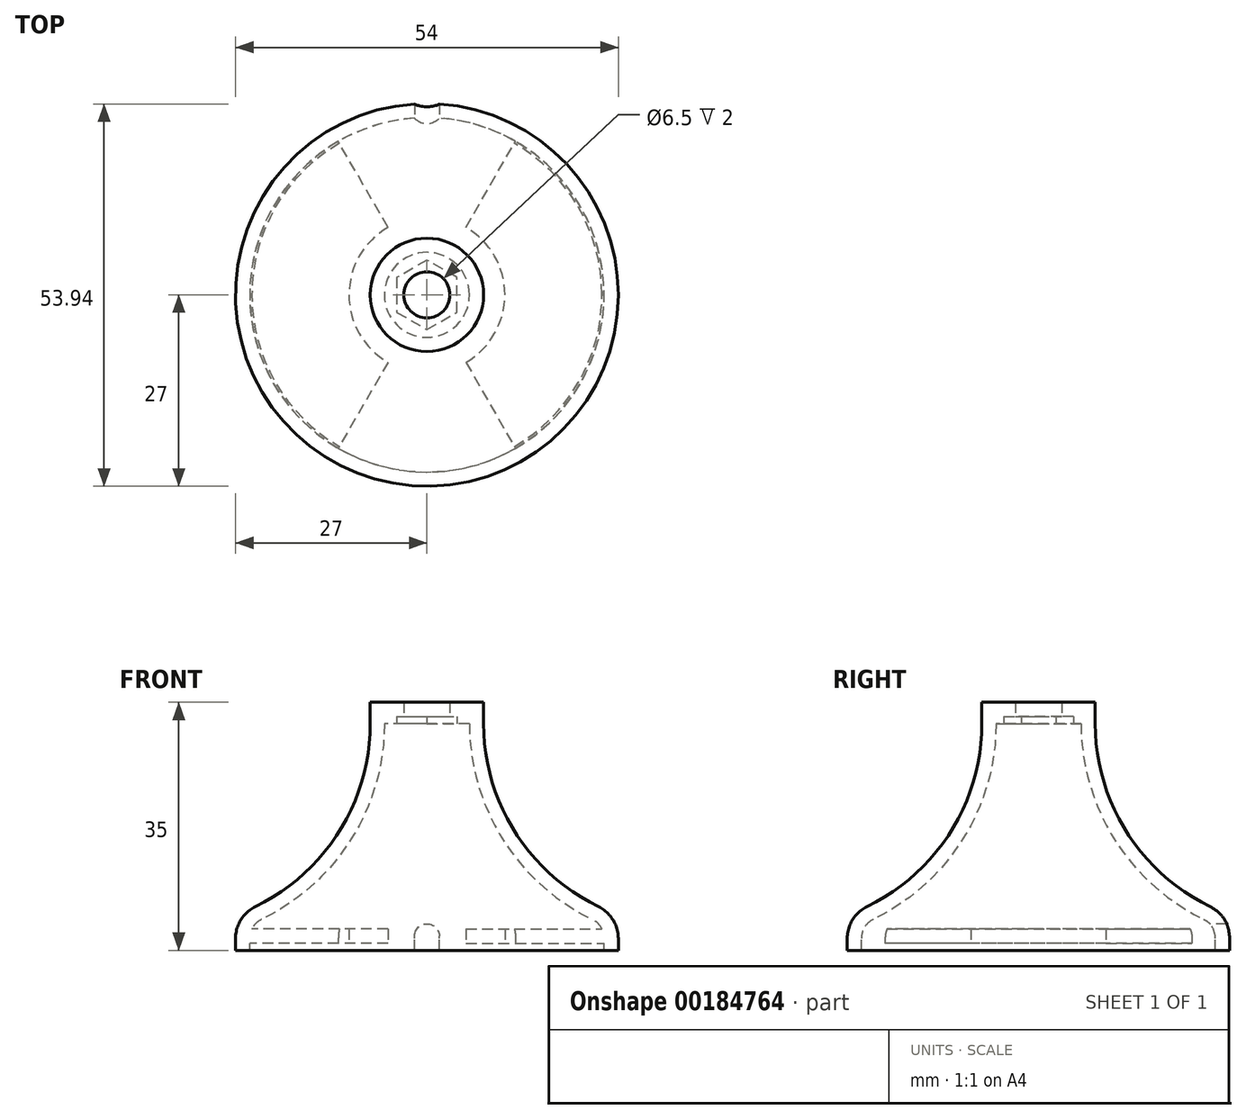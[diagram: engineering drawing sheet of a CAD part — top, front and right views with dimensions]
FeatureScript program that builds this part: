
annotation { "Feature Type Name" : "Feature", "Feature Type Description" : "" }
export const myFeature = defineFeature(function(context is Context, id is Id, definition is map)
    precondition{}
    {
        {
            var Q0;
            Q0=qCreatedBy(makeId("Front.planeOp"),FACE);
            var sketch = newSketch(context, id + "F0", { "sketchPlane" : qUnion([Q0])});
            skLineSegment(sketch, "E0", {"start": v(0, 35) * mm, "end": v(-8, 35) * mm});
            skLineSegment(sketch, "E1", {"start": v(-8, 35) * mm, "end": v(-8, 32) * mm});
            skLineSegment(sketch, "E2", {"start": v(0, 0) * mm, "end": v(-27, 0) * mm, "construction": true});
            skLineSegment(sketch, "E3", {"start": v(-27, 0) * mm, "end": v(-27, 1.68) * mm});
            skLineSegment(sketch, "E4", {"start": v(0, 35) * mm, "end": v(0, 0) * mm, "construction": true});
            skArc(sketch, "E5", {"start": v(-24.18, 6.18) * mm, "mid": v(-12.38, 16.77) * mm, "end": v(-8, 32) * mm});
            skPoint(sketch, "E6.visualSharp", {"position": v(-27, 5) * mm});
            skArc(sketch, "E6.filletArc", {"start": v(-24.18, 6.18) * mm, "mid": v(-26.24, 4.34) * mm, "end": v(-27, 1.68) * mm});
            skLineSegment(sketch, "E7", {"start": v(0, 35) * mm, "end": v(0, 32) * mm});
            skLineSegment(sketch, "E8.0", {"start": v(-25, 0) * mm, "end": v(-25, 1.68) * mm});
            skArc(sketch, "E8.1", {"start": v(-23.3, 4.38) * mm, "mid": v(-10.68, 15.7) * mm, "end": v(-6, 32) * mm});
            skLineSegment(sketch, "E8.2", {"start": v(0, 33) * mm, "end": v(-6.02, 33) * mm, "construction": true});
            skLineSegment(sketch, "E9", {"start": v(-27, 0) * mm, "end": v(-25, 0) * mm});
            skPoint(sketch, "E10.visualSharp", {"position": v(-25, 3.63) * mm});
            skArc(sketch, "E10.filletArc", {"start": v(-23.3, 4.38) * mm, "mid": v(-24.54, 3.28) * mm, "end": v(-25, 1.68) * mm});
            skLineSegment(sketch, "E11", {"start": v(0, 32) * mm, "end": v(-6, 32) * mm});
            skSolve(sketch);
        }
        {
            var Q0;
            Q0 = qSketchRegion(id + "F0", true);
            var Q1;
            Q1=sQuery(id+"F0.wireOp",EDGE,"E4");
            revolve(context, id + "F1", {"entities" : qUnion([Q0]), "axis" : qUnion([Q1]), "revolveType" : RevolveType.FULL});
        }
        {
            var Q0;
            Q0=makeQuery(id+"F1.opRevolve","SWEPT_FACE",FACE,{"disambiguationData":[OSD([sQuery(id+"F0.wireOp",EDGE,"E11")])]});
            var sketch = newSketch(context, id + "F2", { "sketchPlane" : qUnion([Q0])});
            skCircle(sketch, "E12.cCircle", {"center": v(0, 0) * mm, "radius": 4.25 * mm, "construction": true});
            skLineSegment(sketch, "E12.0", {"start": v(4.25, 2.45) * mm, "end": v(4.25, -2.45) * mm});
            skLineSegment(sketch, "E12.1", {"start": v(4.25, -2.45) * mm, "end": v(0, -4.9) * mm});
            skLineSegment(sketch, "E12.2", {"start": v(0, -4.9) * mm, "end": v(-4.25, -2.45) * mm});
            skLineSegment(sketch, "E12.3", {"start": v(-4.25, -2.45) * mm, "end": v(-4.25, 2.45) * mm});
            skLineSegment(sketch, "E12.4", {"start": v(-4.25, 2.45) * mm, "end": v(0, 4.9) * mm});
            skLineSegment(sketch, "E12.5", {"start": v(0, 4.9) * mm, "end": v(4.25, 2.45) * mm});
            skPoint(sketch, "E12.0.midPoint", {"position": v(4.25, 0) * mm});
            skSolve(sketch);
        }
        {
            var Q0;
            Q0 = qSketchRegion(id + "F2", true);
            extrude(context, id + "F3", {"entities" : qUnion([Q0]), "operationType" : NewBodyOperationType.REMOVE, "oppositeDirection" : true, "depth" : 1 * mm});
        }
        {
            var Q0;
            Q0=makeQuery(id+"F3.boolean.opBoolean","COPY",FACE,{"derivedFrom":makeQuery(id+"F3.opExtrude","CAP_FACE",FACE,{"disambiguationData":[OSD([sQuery(id+"F2.wireOp",EDGE,"E12.0"),sQuery(id+"F2.wireOp",EDGE,"E12.1"),sQuery(id+"F2.wireOp",EDGE,"E12.2"),sQuery(id+"F2.wireOp",EDGE,"E12.3"),sQuery(id+"F2.wireOp",EDGE,"E12.4"),sQuery(id+"F2.wireOp",EDGE,"E12.5")])],"isStart":false})});
            var sketch = newSketch(context, id + "F4", { "sketchPlane" : qUnion([Q0])});
            skCircle(sketch, "E13", {"center": v(0, 0) * mm, "radius": 3.25 * mm});
            skSolve(sketch);
        }
        {
            var Q0;
            Q0 = qSketchRegion(id + "F4", true);
            extrude(context, id + "F5", {"entities" : qUnion([Q0]), "operationType" : NewBodyOperationType.REMOVE, "endBound" : BoundingType.THROUGH_ALL, "oppositeDirection" : true, "depth" : 25 * mm});
        }
        {
            var Q0;
            Q0=makeQuery(id+"F1.opRevolve","SWEPT_FACE",FACE,{"disambiguationData":[OSD([sQuery(id+"F0.wireOp",EDGE,"E9")])]});
            cPlane(context, id + "F6", {"entities" : qUnion([Q0]), "cplaneType" : CPlaneType.OFFSET, "offset" : 1 * mm, "oppositeDirection" : true, "width" : 150 * mm, "height" : 150 * mm});
        }
        {
            var Q0;
            Q0=qCreatedBy(id+"F6.planeOp",FACE);
            var sketch = newSketch(context, id + "F7", { "sketchPlane" : qUnion([Q0])});
            skArc(sketch, "E14", {"start": v(12.5, -21.65) * mm, "mid": v(25, 0) * mm, "end": v(12.5, 21.65) * mm});
            skLineSegment(sketch, "E15", {"start": v(5.5, 9.53) * mm, "end": v(12.5, 21.65) * mm});
            skLineSegment(sketch, "E16.MirrorCS", {"start": v(5.5, -9.53) * mm, "end": v(12.5, -21.65) * mm});
            skArc(sketch, "E17", {"start": v(5.5, -9.53) * mm, "mid": v(11, 0) * mm, "end": v(5.5, 9.53) * mm});
            skArc(sketch, "E18.MirrorCS", {"start": v(-12.5, -21.65) * mm, "mid": v(-25, 0) * mm, "end": v(-12.5, 21.65) * mm});
            skLineSegment(sketch, "E19.MirrorCS", {"start": v(-5.5, 9.53) * mm, "end": v(-12.5, 21.65) * mm});
            skArc(sketch, "E20.MirrorCS", {"start": v(-5.5, -9.53) * mm, "mid": v(-11, 0) * mm, "end": v(-5.5, 9.53) * mm});
            skLineSegment(sketch, "E21.MirrorCS", {"start": v(-5.5, -9.53) * mm, "end": v(-12.5, -21.65) * mm});
            skSolve(sketch);
        }
        {
            var Q0;
            Q0 = qSketchRegion(id + "F7", true);
            extrude(context, id + "F8", {"entities" : qUnion([Q0]), "operationType" : NewBodyOperationType.ADD, "oppositeDirection" : true, "depth" : 2 * mm});
        }
        {
            var Q0;
            Q0=qCreatedBy(makeId("Front.planeOp"),FACE);
            var sketch = newSketch(context, id + "F9", { "sketchPlane" : qUnion([Q0])});
            skArc(sketch, "E22", {"start": v(1.75, 2) * mm, "mid": v(0, 3.75) * mm, "end": v(-1.75, 2) * mm});
            skLineSegment(sketch, "E23", {"start": v(-1.75, 2) * mm, "end": v(-1.75, 0) * mm});
            skLineSegment(sketch, "E24", {"start": v(1.75, 2) * mm, "end": v(1.75, 0) * mm});
            skLineSegment(sketch, "E25", {"start": v(-1.75, 0) * mm, "end": v(1.75, 0) * mm});
            skSolve(sketch);
        }
        {
            var Q0;
            Q0 = qSketchRegion(id + "F9", true);
            extrude(context, id + "F10", {"entities" : qUnion([Q0]), "operationType" : NewBodyOperationType.REMOVE, "endBound" : BoundingType.THROUGH_ALL, "oppositeDirection" : true, "depth" : 25 * mm});
        }
    });
